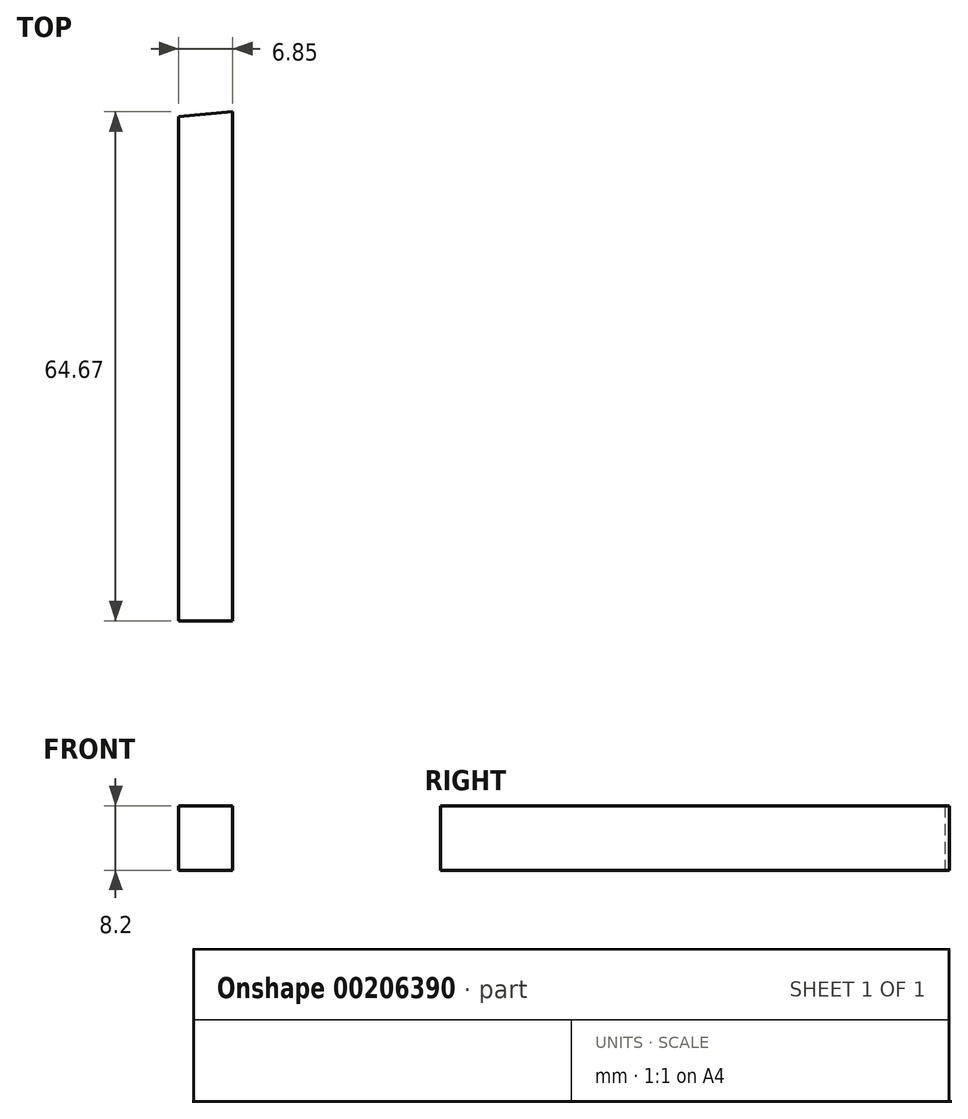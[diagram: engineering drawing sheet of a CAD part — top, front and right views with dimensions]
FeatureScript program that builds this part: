
annotation { "Feature Type Name" : "Feature", "Feature Type Description" : "" }
export const myFeature = defineFeature(function(context is Context, id is Id, definition is map)
    precondition{}
    {
        {
            var Q0;
            Q0=qCreatedBy(makeId("Top.planeOp"),FACE);
            var sketch = newSketch(context, id + "F0", { "sketchPlane" : qUnion([Q0])});
            skLineSegment(sketch, "E0", {"start": v(-59, 36.8) * mm, "end": v(-59, -27.27) * mm});
            skLineSegment(sketch, "E1", {"start": v(-59, -27.27) * mm, "end": v(-52.15, -27.27) * mm});
            skLineSegment(sketch, "E2", {"start": v(-52.15, -27.27) * mm, "end": v(-52.15, 37.4) * mm});
            skLineSegment(sketch, "E3", {"start": v(-52.15, 37.4) * mm, "end": v(-59, 36.8) * mm});
            skSolve(sketch);
        }
        {
            var Q0;
            Q0 = qSketchRegion(id + "F0", true);
            extrude(context, id + "F1", {"entities" : qUnion([Q0]), "depth" : 8.2 * mm});
        }
    });
